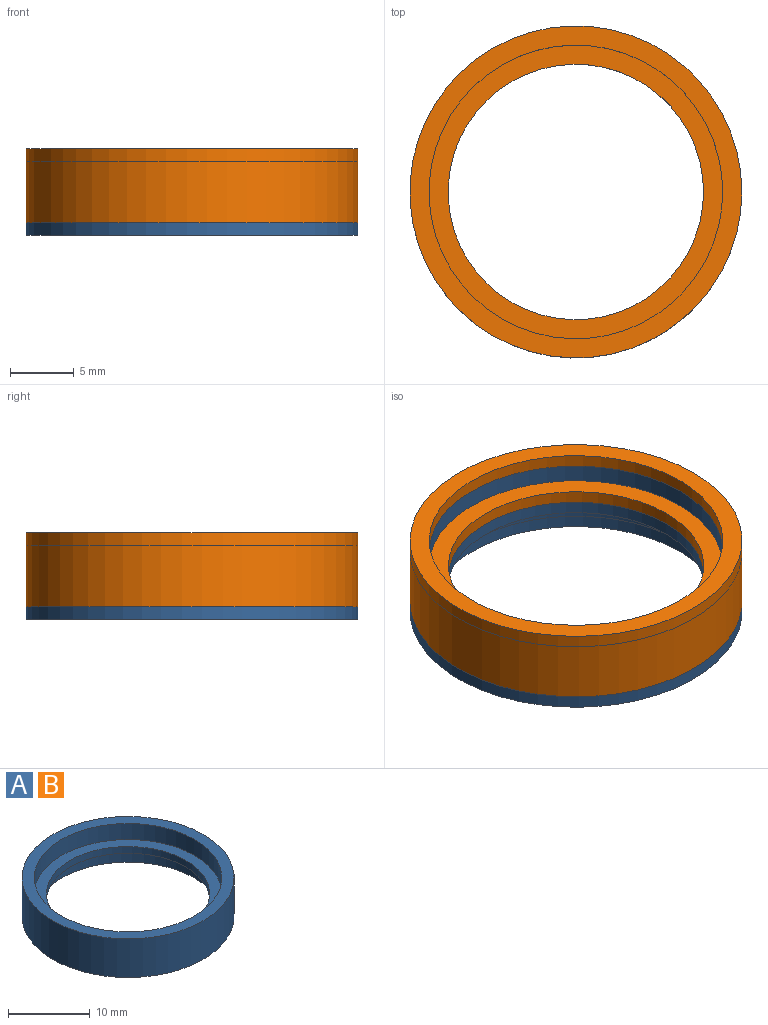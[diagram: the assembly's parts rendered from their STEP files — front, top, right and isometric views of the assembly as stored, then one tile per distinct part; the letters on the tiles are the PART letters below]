
ASSEMBLY  parts=2 mates=1
PART A: 8 faces, bbox 26x26x5.8 mm
  f0: plane 23x23mm, normal (0,0,-1), area 101.3mm2, adj f4,f6
  f1: cylinder r=11.5mm len=23mm, axis (0,0,-1), area 173.4mm2, adj f3,f5
  f2: cylinder r=13mm len=26mm, axis (0,0,-1), area 473.8mm2, adj f3,f7
  f3: plane 26x26mm, normal (0,0,1), area 115.5mm2, adj f1,f2
  f4: cylinder r=10mm len=20mm, axis (0,0,-1), area 62.8mm2, adj f0,f5
  f5: plane 23x23mm, normal (0,0,1), area 101.3mm2, adj f1,f4
  f6: cylinder r=11.5mm len=23mm, axis (0,0,1), area 173.4mm2, adj f0,f7
  f7: plane 26x26mm, normal (0,0,-1), area 115.5mm2, adj f2,f6
PART B: same geometry as A
PLACE A rot(axis=(1,0,0),180deg) t=(5.17,5.05,1.59)mm
PLACE B t=(5.17,5.05,1.59)mm
MATE planar A.f2 <-> B.f2  axis (0,0,1) through (5.17,5.05,1.59)mm
